# Revit family: R-MTF-271
name_source: partatom
category: Modèles génériques
units: mm (PartAtom-declared; Revit-internal decimal feet)

## family parameters
Conserver l'orientation des annotations = Non
Cote de connecteur circulaire = Utiliser le diamètre
Couper avec des vides une fois chargée = Non
Hôte = Sol
Partagée = Non
Peut héberger une armature = Non
Repère de localisation dans la pièce = Non
Toujours verticalement = Oui
Type d'élément = Normal

## types (1)
- MTF-271
    1V = Oui
    2V = Non
    Ame = Acier AISI 1015
    DAS = Non
    Description = Trappe de visite M 601 TH 1 vantail horizontale, EI60, avec cadre/huisserie métal
    Elévation par défaut = 0 mm  [stored 0 ft]
    Ep parement = 2 mm  [stored 0.00656168 ft]
    Ep porte = 51 mm  [stored 0.167323 ft]
    Fabricant = MALERBA
    Fiche_Produit = MTF-271
    Largeur passage libre = 1120 mm  [stored 3.67454 ft]
    Modèle = 01-Trappe
    Note d'identification = 1V EI60 - TRAPPE HORIZONTALE
    Parement = Peinture Laquée PMT - Gris Argent Métal - RAL 9006
    Plat = Non
    Plat 2 = Oui
    Reference_Commerciale = M 601 TH
    Resistance_Feu = EI60
    Sens_Feu = Dessous (opposé aux pivots)
    URL = https://www.malerba.fr
    X_Dc lP/2 = 1125 mm
    X_LO = 1180 mm  [stored 3.87139 ft]
    X_LP/2 = 600 mm  [stored 1.9685 ft]
    X_Largeur hors tout = 40 mm  [stored 0.131234 ft]
    X_lP = 1120 mm  [stored 3.67454 ft]

note: [stored X ft] marks values corroborated as IEEE doubles in the binary element streams (Revit-internal decimal feet)

## geometry (parser evidence)
native form markers: Blend x12
no freeform markers — native parametric forms only
